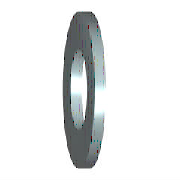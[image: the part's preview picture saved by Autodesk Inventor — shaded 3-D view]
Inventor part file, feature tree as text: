
AUTODESK INVENTOR PART (.ipt)
format: ipt  version: 2023 (Build 270158000, 158)  size: 106,496 bytes
history: native  units: mm (DEFAULTED — no unit token found)
features: extrude x1, other x1, plane x1, sketch x1
ambient origin geometry x7: Origin, YZ Plane, XY Plane, X Axis, Y Axis, Z Axis, Center Point
bodies: Solid1 (feature_tree)
feature tree (4):
  extrude  "Corpo"  Depth=19.0mm
  other  "Work Axis1"
  plane  "Work Plane1"
  sketch  "Schizzo"
